# Revit family: Power-ModularDevices-GEWISS-90AM-CONTACTORS_20A_2M
name_source: partatom
category: Apparecchi elettrici
revit_build: Autodesk Revit 2016 (Build: 20161004_0715(x64)
units: mm (PartAtom-declared; Revit-internal decimal feet)

## family parameters
Condiviso = No
Host = Superficie
Mantenere orientamento annotazione = Sì
Numero OmniClass = 23.80.30.00
Punto di calcolo locali = Sì
Quota connettore circolare = Usa diametro
Taglio con vuoti quando caricato = No
Tipo di parte = Normale
Titolo OmniClass = Distribution Devices

## types (2) — shared parameters
A = 36 mm  [stored 0.11811 ft]
B = 85 mm  [stored 0.278871 ft]
C = 65 mm  [stored 0.213255 ft]
Catalogue = POWER
Catalogue Range = 90 AM
Control coil voltage (V) = 230Vac
D = 45 mm  [stored 0.147638 ft]
Dist_dalla barra din = 5 mm  [stored 0.0164042 ft]
Electrocod = 1712
Fin_contattore = <Per categoria>
IDF = b7117b48-3d7f-414b-b3b5-8ec2a2a25e34
IDT = 6c888b2f-99e0-476a-b92d-ad9b1437b277
Immagine tipo = GWD6709.jpg
No. Chorus modules = 2
Numero poli = 1
Potenza in Watt = 0 V
Produttore = GEWISS S.p.A.
Prospetto di default = 1219 mm
Rated current (AC-1/AC-7a) = 20 A - CTR20
TEXT LABEL = A
Technical sheet = https://www.gewiss.com
URL = https://www.gewiss.com
Version file RFA = 18.0

## per-type parameters (varying)
| type | Descrizione | EAN code | Modello |
| GWD6708 - CONTACTOR 20A 3NO 230V 2M | CONTACTOR 20A 3NO 230V 2M | 8011564809437 | GWD6708 |
| GWD6709 - CONTACTOR 20A 4NO 230V 2M | CONTACTOR 20A 4NO 230V 2M | 8011564809444 | GWD6709 |

note: [stored X ft] marks values corroborated as IEEE doubles in the binary element streams (Revit-internal decimal feet)
